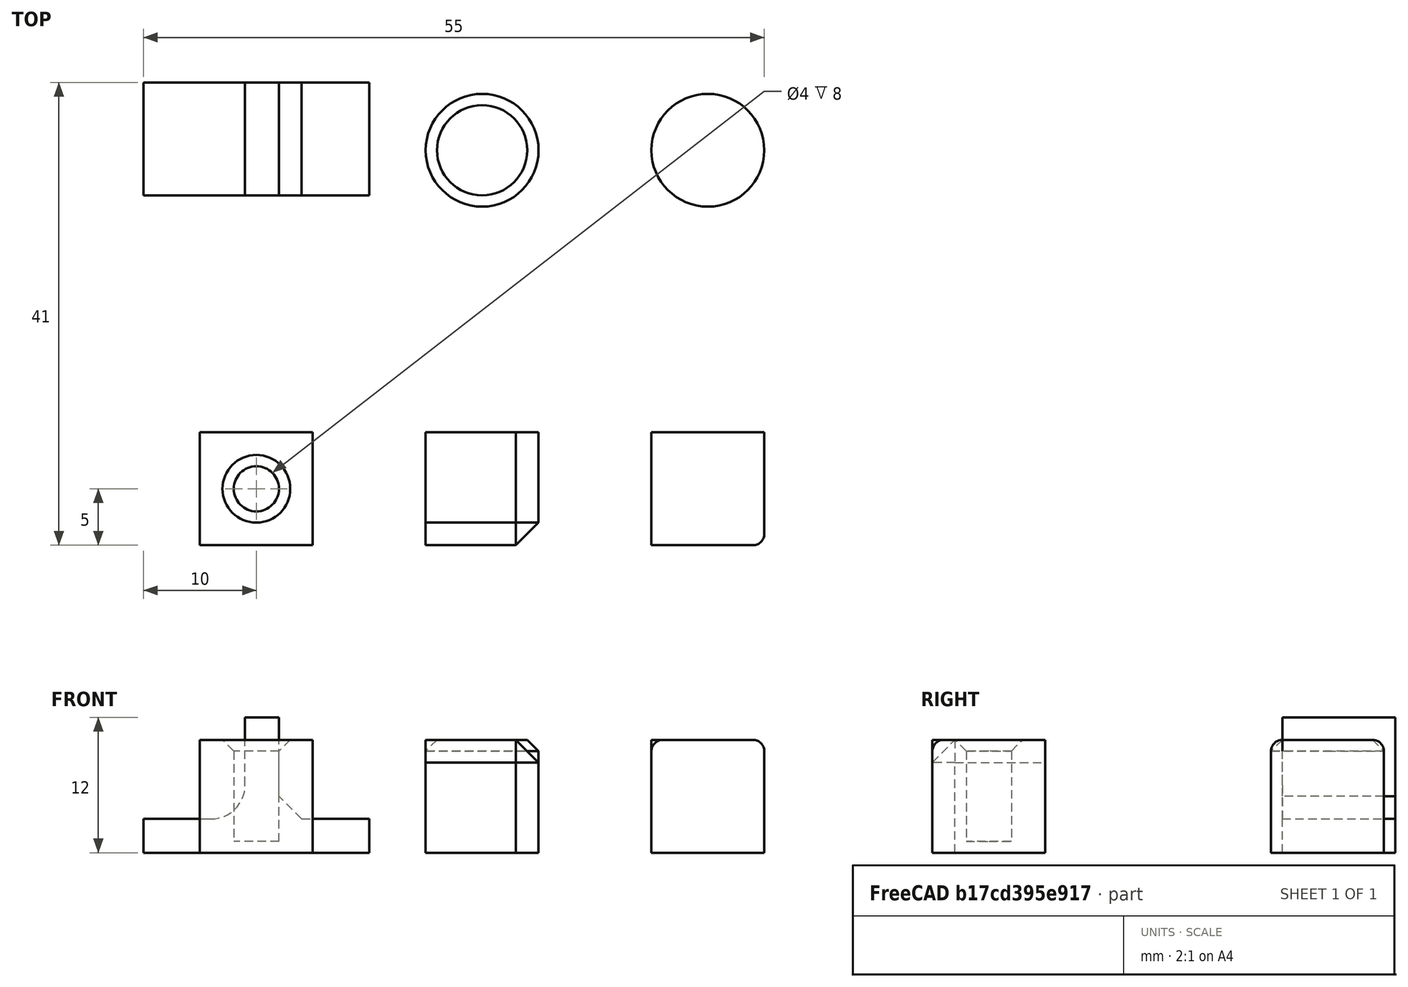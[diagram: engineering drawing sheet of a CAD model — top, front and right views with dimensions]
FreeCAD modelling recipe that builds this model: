
FCSTD DOCUMENT  (FreeCAD 0.21R33694 (Git))
Label: OJT1_T012P011_figures
License: All rights reserved
LicenseURL: http://en.wikipedia.org/wiki/All_rights_reserved
objects: Part::Box×5, Part::Chamfer×4, Part::Cylinder×3, Part::Fillet×3, Part::Cut×1, Part::MultiFuse×1
note: 17 computed .brp shape members not serialized (recipe doc carries the construction recipe); baked Part::Feature solids carry a one-line shape summary decoded from their .brp

FEATURE [Part::Box] Box  label="cubo1"
  AttacherType = Attacher::AttachEngine3D
  Height = 10
  Length = 10
  Placement = pos=(20,0,0) rot=(0,0,1;0rad)
  Width = 10
FEATURE [Part::Box] Box001  label="cubo2"
  AttacherType = Attacher::AttachEngine3D
  Height = 10
  Length = 10
  Placement = pos=(40,0,0) rot=(0,0,1;0rad)
  Width = 10
FEATURE [Part::Box] Box002  label="cubo3"
  AttacherType = Attacher::AttachEngine3D
  Height = 10
  Length = 10
  Placement = pos=(-5,-5,0) rot=(0,0,1;0rad)
  Width = 10
FEATURE [Part::Cylinder] Cylinder
  Angle = 360
  AttacherType = Attacher::AttachEngine3D
  FirstAngle = 0
  Height = 10
  Placement = pos=(0,0,1) rot=(0,0,1;0rad)
  Radius = 2
  SecondAngle = 0
FEATURE [Part::Cut] Cut
  Base = -> Box002
  Placement = pos=(5,5,0) rot=(0,0,1;0rad)
  Refine = true
  Tool = -> Cylinder
FEATURE [Part::Cylinder] Cylinder001  label="cilindre1"
  Angle = 360
  AttacherType = Attacher::AttachEngine3D
  FirstAngle = 0
  Height = 10
  Placement = pos=(45,35,0) rot=(0,0,1;0rad)
  Radius = 5
  SecondAngle = 0
FEATURE [Part::Cylinder] Cylinder002  label="cilindre2"
  Angle = 360
  AttacherType = Attacher::AttachEngine3D
  FirstAngle = 0
  Height = 10
  Placement = pos=(25,35,0) rot=(0,0,1;0rad)
  Radius = 5
  SecondAngle = 0
FEATURE [Part::Box] Box003  label="base"
  AttacherType = Attacher::AttachEngine3D
  Height = 3
  Length = 20
  Width = 10
FEATURE [Part::Box] Box004  label="cub"
  AttacherType = Attacher::AttachEngine3D
  Height = 12
  Length = 3
  Placement = pos=(9,0,0) rot=(0,0,1;0rad)
  Width = 10
FEATURE [Part::MultiFuse] Fusion
  Placement = pos=(-5,31,0) rot=(0,0,1;0rad)
  Refine = true
  Shapes = -> [Box004,Box003]
FEATURE [Part::Fillet] Fillet
  Base = -> Box001
  Edges = 3 edges r=1: [Edge5,Edge6,Edge10]
FEATURE [Part::Chamfer] Chamfer
  Base = -> Box
  Edges = 3 edges r=2: [Edge5,Edge6,Edge10]
FEATURE [Part::Chamfer] Chamfer001
  Base = -> Cut
  Edges = 1 edges r=1: [Edge10]
FEATURE [Part::Fillet] Fillet001
  Base = -> Cylinder001
  Edges = 1 edges r=1: [Edge3]
FEATURE [Part::Chamfer] Chamfer002
  Base = -> Cylinder002
  Edges = 1 edges r=1: [Edge3]
FEATURE [Part::Chamfer] Chamfer003
  Base = -> Fusion
  Edges = 1 edges r=2: [Edge7]
FEATURE [Part::Fillet] Fillet002
  Base = -> Chamfer003
  Edges = 1 edges r=3: [Edge25]
